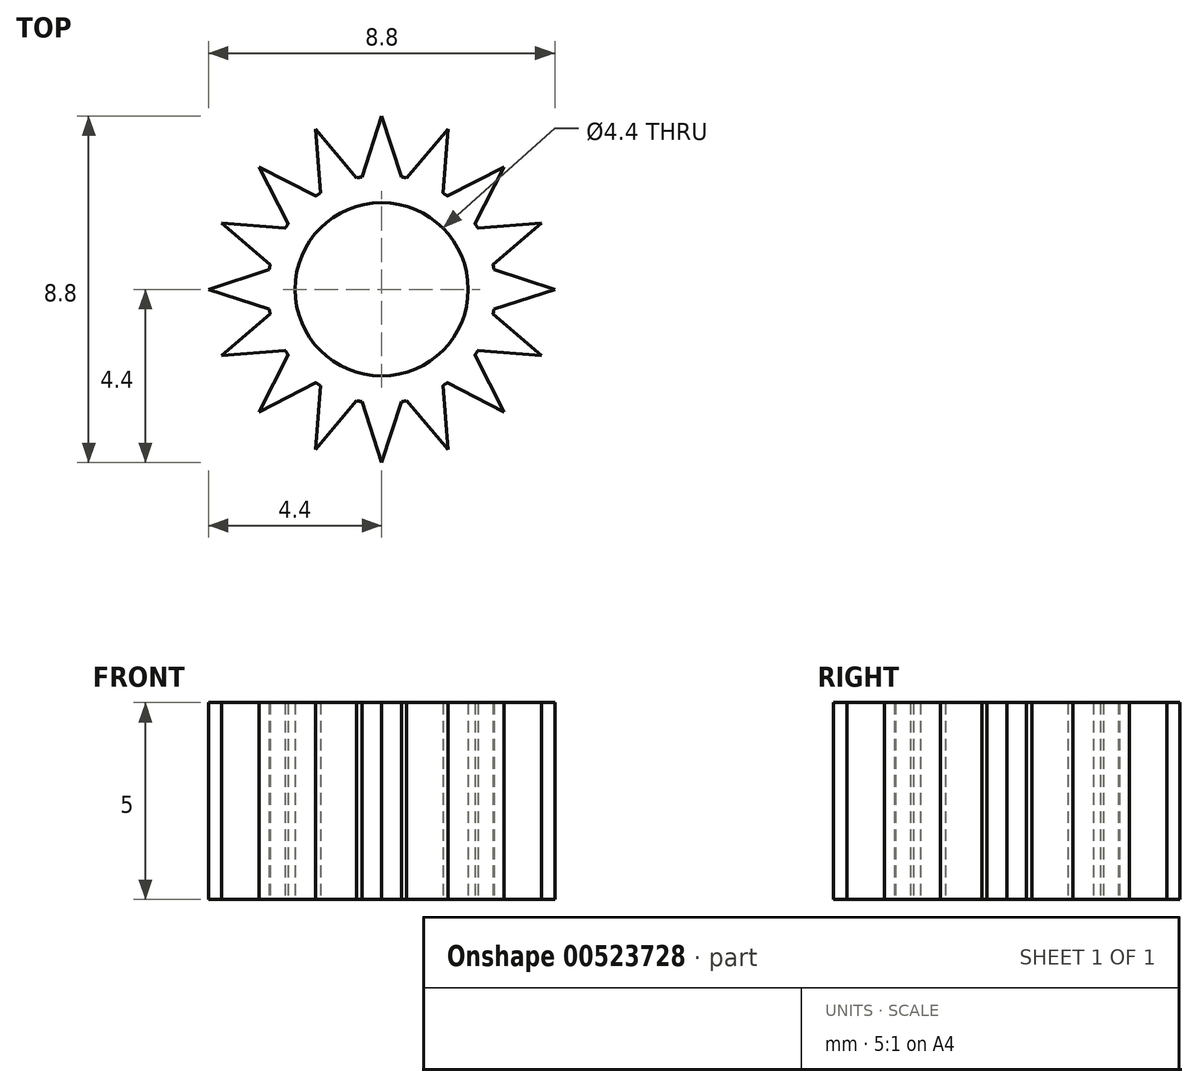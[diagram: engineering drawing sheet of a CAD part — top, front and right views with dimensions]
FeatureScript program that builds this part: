
annotation { "Feature Type Name" : "Feature", "Feature Type Description" : "" }
export const myFeature = defineFeature(function(context is Context, id is Id, definition is map)
    precondition{}
    {
        {
            var Q0;
            Q0=qCreatedBy(makeId("Top.planeOp"),FACE);
            var sketch = newSketch(context, id + "F0", { "sketchPlane" : qUnion([Q0])});
            skCircle(sketch, "E0", {"center": v(0, 0) * mm, "radius": 2.9 * mm});
            skCircle(sketch, "E1", {"center": v(0, 0) * mm, "radius": 2.2 * mm});
            skLineSegment(sketch, "E2", {"start": v(0, 2.9) * mm, "end": v(0.5, 2.9) * mm, "construction": true});
            skLineSegment(sketch, "E3", {"start": v(0.5, 2.9) * mm, "end": v(-0.5, 2.9) * mm, "construction": true});
            skLineSegment(sketch, "E4", {"start": v(-0.5, 2.9) * mm, "end": v(-0.5, 2.64) * mm, "construction": true});
            skLineSegment(sketch, "E5", {"start": v(0.5, 2.9) * mm, "end": v(0.5, 2.58) * mm, "construction": true});
            skLineSegment(sketch, "E6", {"start": v(0, 2.9) * mm, "end": v(0, 4.4) * mm, "construction": true});
            skLineSegment(sketch, "E7", {"start": v(-0.5, 2.86) * mm, "end": v(0, 4.4) * mm});
            skLineSegment(sketch, "E8", {"start": v(0.5, 2.86) * mm, "end": v(0, 4.4) * mm});
            skLineSegment(sketch, "E9.1.0", {"start": v(-0.63, 2.83) * mm, "end": v(-1.68, 4.07) * mm});
            skLineSegment(sketch, "E9.1.1", {"start": v(-1.56, 2.45) * mm, "end": v(-1.68, 4.07) * mm});
            skLineSegment(sketch, "E9.2.0", {"start": v(-1.67, 2.37) * mm, "end": v(-3.11, 3.11) * mm});
            skLineSegment(sketch, "E9.2.1", {"start": v(-2.37, 1.67) * mm, "end": v(-3.11, 3.11) * mm});
            skLineSegment(sketch, "E9.3.0", {"start": v(-2.45, 1.56) * mm, "end": v(-4.07, 1.68) * mm});
            skLineSegment(sketch, "E9.3.1", {"start": v(-2.83, 0.63) * mm, "end": v(-4.07, 1.68) * mm});
            skLineSegment(sketch, "E9.4.0", {"start": v(-2.86, 0.5) * mm, "end": v(-4.4, 0) * mm});
            skLineSegment(sketch, "E9.4.1", {"start": v(-2.86, -0.5) * mm, "end": v(-4.4, 0) * mm});
            skLineSegment(sketch, "E9.5.0", {"start": v(-2.83, -0.63) * mm, "end": v(-4.07, -1.68) * mm});
            skLineSegment(sketch, "E9.5.1", {"start": v(-2.45, -1.56) * mm, "end": v(-4.07, -1.68) * mm});
            skLineSegment(sketch, "E9.6.0", {"start": v(-2.37, -1.67) * mm, "end": v(-3.11, -3.11) * mm});
            skLineSegment(sketch, "E9.6.1", {"start": v(-1.67, -2.37) * mm, "end": v(-3.11, -3.11) * mm});
            skLineSegment(sketch, "E9.7.0", {"start": v(-1.56, -2.45) * mm, "end": v(-1.68, -4.07) * mm});
            skLineSegment(sketch, "E9.7.1", {"start": v(-0.63, -2.83) * mm, "end": v(-1.68, -4.07) * mm});
            skLineSegment(sketch, "E9.8.0", {"start": v(-0.5, -2.86) * mm, "end": v(0, -4.4) * mm});
            skLineSegment(sketch, "E9.8.1", {"start": v(0.5, -2.86) * mm, "end": v(0, -4.4) * mm});
            skLineSegment(sketch, "E9.9.0", {"start": v(0.63, -2.83) * mm, "end": v(1.68, -4.07) * mm});
            skLineSegment(sketch, "E9.9.1", {"start": v(1.56, -2.45) * mm, "end": v(1.68, -4.07) * mm});
            skLineSegment(sketch, "E9.10.0", {"start": v(1.67, -2.37) * mm, "end": v(3.11, -3.11) * mm});
            skLineSegment(sketch, "E9.10.1", {"start": v(2.37, -1.67) * mm, "end": v(3.11, -3.11) * mm});
            skLineSegment(sketch, "E9.11.0", {"start": v(2.45, -1.56) * mm, "end": v(4.07, -1.68) * mm});
            skLineSegment(sketch, "E9.11.1", {"start": v(2.83, -0.63) * mm, "end": v(4.07, -1.68) * mm});
            skLineSegment(sketch, "E9.12.0", {"start": v(2.86, -0.5) * mm, "end": v(4.4, 0) * mm});
            skLineSegment(sketch, "E9.12.1", {"start": v(2.86, 0.5) * mm, "end": v(4.4, 0) * mm});
            skLineSegment(sketch, "E9.13.0", {"start": v(2.83, 0.63) * mm, "end": v(4.07, 1.68) * mm});
            skLineSegment(sketch, "E9.13.1", {"start": v(2.45, 1.56) * mm, "end": v(4.07, 1.68) * mm});
            skLineSegment(sketch, "E9.14.0", {"start": v(2.37, 1.67) * mm, "end": v(3.11, 3.11) * mm});
            skLineSegment(sketch, "E9.14.1", {"start": v(1.67, 2.37) * mm, "end": v(3.11, 3.11) * mm});
            skLineSegment(sketch, "E9.15.0", {"start": v(1.56, 2.45) * mm, "end": v(1.68, 4.07) * mm});
            skLineSegment(sketch, "E9.15.1", {"start": v(0.63, 2.83) * mm, "end": v(1.68, 4.07) * mm});
            skSolve(sketch);
        }
        {
            var Q0;
            Q0=makeQuery(id+"F0.imprint","IMPRINT",FACE,{"disambiguationData":[TD([[makeQuery(id+"F0.imprint","IMPRINT",EDGE,{"derivedFrom":sQuery(id+"F0.wireOp",EDGE,"E1")}),-1.0]])]});
            var Q1;
            {var subQ0=sQuery(id+"F0.wireOp",EDGE,"E7");Q1=makeQuery(id+"F0.imprint","IMPRINT",FACE,{"disambiguationData":[TD([[makeQuery(id+"F0.imprint","IMPRINT",EDGE,{"derivedFrom":subQ0}),-1.0]])]});}
            var Q2;
            {var subQ0=sQuery(id+"F0.wireOp",EDGE,"E9.15.0");Q2=makeQuery(id+"F0.imprint","IMPRINT",FACE,{"disambiguationData":[TD([[makeQuery(id+"F0.imprint","IMPRINT",EDGE,{"derivedFrom":subQ0}),1.0]])]});}
            var Q3;
            {var subQ0=sQuery(id+"F0.wireOp",EDGE,"E9.14.0");Q3=makeQuery(id+"F0.imprint","IMPRINT",FACE,{"disambiguationData":[TD([[makeQuery(id+"F0.imprint","IMPRINT",EDGE,{"derivedFrom":subQ0}),1.0]])]});}
            var Q4;
            {var subQ0=sQuery(id+"F0.wireOp",EDGE,"E9.13.0");Q4=makeQuery(id+"F0.imprint","IMPRINT",FACE,{"disambiguationData":[TD([[makeQuery(id+"F0.imprint","IMPRINT",EDGE,{"derivedFrom":subQ0}),1.0]])]});}
            var Q5;
            {var subQ0=sQuery(id+"F0.wireOp",EDGE,"E9.12.0");Q5=makeQuery(id+"F0.imprint","IMPRINT",FACE,{"disambiguationData":[TD([[makeQuery(id+"F0.imprint","IMPRINT",EDGE,{"derivedFrom":subQ0}),1.0]])]});}
            var Q6;
            {var subQ0=sQuery(id+"F0.wireOp",EDGE,"E9.11.0");Q6=makeQuery(id+"F0.imprint","IMPRINT",FACE,{"disambiguationData":[TD([[makeQuery(id+"F0.imprint","IMPRINT",EDGE,{"derivedFrom":subQ0}),1.0]])]});}
            var Q7;
            {var subQ0=sQuery(id+"F0.wireOp",EDGE,"E9.10.0");Q7=makeQuery(id+"F0.imprint","IMPRINT",FACE,{"disambiguationData":[TD([[makeQuery(id+"F0.imprint","IMPRINT",EDGE,{"derivedFrom":subQ0}),1.0]])]});}
            var Q8;
            {var subQ0=sQuery(id+"F0.wireOp",EDGE,"E9.9.0");Q8=makeQuery(id+"F0.imprint","IMPRINT",FACE,{"disambiguationData":[TD([[makeQuery(id+"F0.imprint","IMPRINT",EDGE,{"derivedFrom":subQ0}),1.0]])]});}
            var Q9;
            {var subQ0=sQuery(id+"F0.wireOp",EDGE,"E9.8.0");Q9=makeQuery(id+"F0.imprint","IMPRINT",FACE,{"disambiguationData":[TD([[makeQuery(id+"F0.imprint","IMPRINT",EDGE,{"derivedFrom":subQ0}),1.0]])]});}
            var Q10;
            {var subQ0=sQuery(id+"F0.wireOp",EDGE,"E9.7.0");Q10=makeQuery(id+"F0.imprint","IMPRINT",FACE,{"disambiguationData":[TD([[makeQuery(id+"F0.imprint","IMPRINT",EDGE,{"derivedFrom":subQ0}),1.0]])]});}
            var Q11;
            {var subQ0=sQuery(id+"F0.wireOp",EDGE,"E9.6.0");Q11=makeQuery(id+"F0.imprint","IMPRINT",FACE,{"disambiguationData":[TD([[makeQuery(id+"F0.imprint","IMPRINT",EDGE,{"derivedFrom":subQ0}),1.0]])]});}
            var Q12;
            {var subQ0=sQuery(id+"F0.wireOp",EDGE,"E9.5.0");Q12=makeQuery(id+"F0.imprint","IMPRINT",FACE,{"disambiguationData":[TD([[makeQuery(id+"F0.imprint","IMPRINT",EDGE,{"derivedFrom":subQ0}),1.0]])]});}
            var Q13;
            {var subQ0=sQuery(id+"F0.wireOp",EDGE,"E9.3.0");Q13=makeQuery(id+"F0.imprint","IMPRINT",FACE,{"disambiguationData":[TD([[makeQuery(id+"F0.imprint","IMPRINT",EDGE,{"derivedFrom":subQ0}),1.0]])]});}
            var Q14;
            {var subQ0=sQuery(id+"F0.wireOp",EDGE,"E9.2.0");Q14=makeQuery(id+"F0.imprint","IMPRINT",FACE,{"disambiguationData":[TD([[makeQuery(id+"F0.imprint","IMPRINT",EDGE,{"derivedFrom":subQ0}),1.0]])]});}
            var Q15;
            {var subQ0=sQuery(id+"F0.wireOp",EDGE,"E9.4.0");Q15=makeQuery(id+"F0.imprint","IMPRINT",FACE,{"disambiguationData":[TD([[makeQuery(id+"F0.imprint","IMPRINT",EDGE,{"derivedFrom":subQ0}),1.0]])]});}
            var Q16;
            {var subQ0=sQuery(id+"F0.wireOp",EDGE,"E9.1.0");Q16=makeQuery(id+"F0.imprint","IMPRINT",FACE,{"disambiguationData":[TD([[makeQuery(id+"F0.imprint","IMPRINT",EDGE,{"derivedFrom":subQ0}),1.0]])]});}
            extrude(context, id + "F1", {"entities" : qUnion([Q0, Q1, Q2, Q3, Q4, Q5, Q6, Q7, Q8, Q9, Q10, Q11, Q12, Q13, Q14, Q15, Q16]), "depth" : 5 * mm, "offsetDistance" : 25 * mm});
        }
    });
